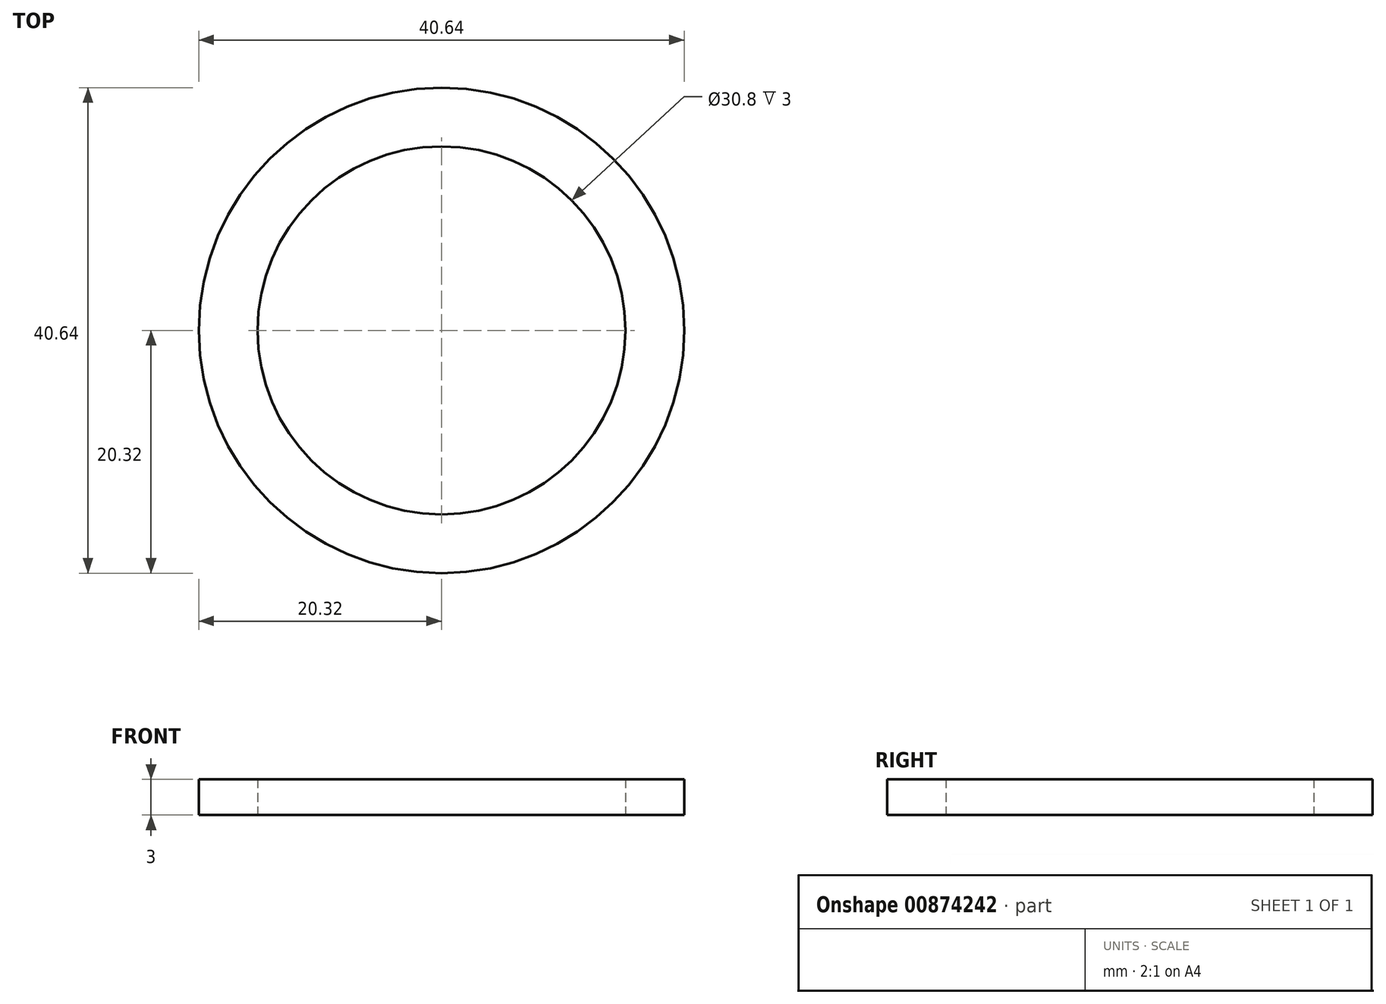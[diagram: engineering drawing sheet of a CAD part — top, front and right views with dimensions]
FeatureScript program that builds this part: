
annotation { "Feature Type Name" : "Feature", "Feature Type Description" : "" }
export const myFeature = defineFeature(function(context is Context, id is Id, definition is map)
    precondition{}
    {
        {
            var Q0;
            Q0=qCreatedBy(makeId("Top.planeOp"),FACE);
            var sketch = newSketch(context, id + "F0", { "sketchPlane" : qUnion([Q0])});
            skCircle(sketch, "E0", {"center": v(0, 0) * mm, "radius": 20.32 * mm});
            skCircle(sketch, "E1", {"center": v(0, 0) * mm, "radius": 15.4 * mm});
            skSolve(sketch);
        }
        {
            var Q0;
            Q0=makeQuery(id+"F0.imprint","IMPRINT",FACE,{"disambiguationData":[TD([[makeQuery(id+"F0.imprint","IMPRINT",EDGE,{"derivedFrom":sQuery(id+"F0.wireOp",EDGE,"E0")}),1.0]])]});
            extrude(context, id + "F1", {"entities" : qUnion([Q0]), "depth" : 3 * mm, "offsetDistance" : 25.4 * mm});
        }
    });
